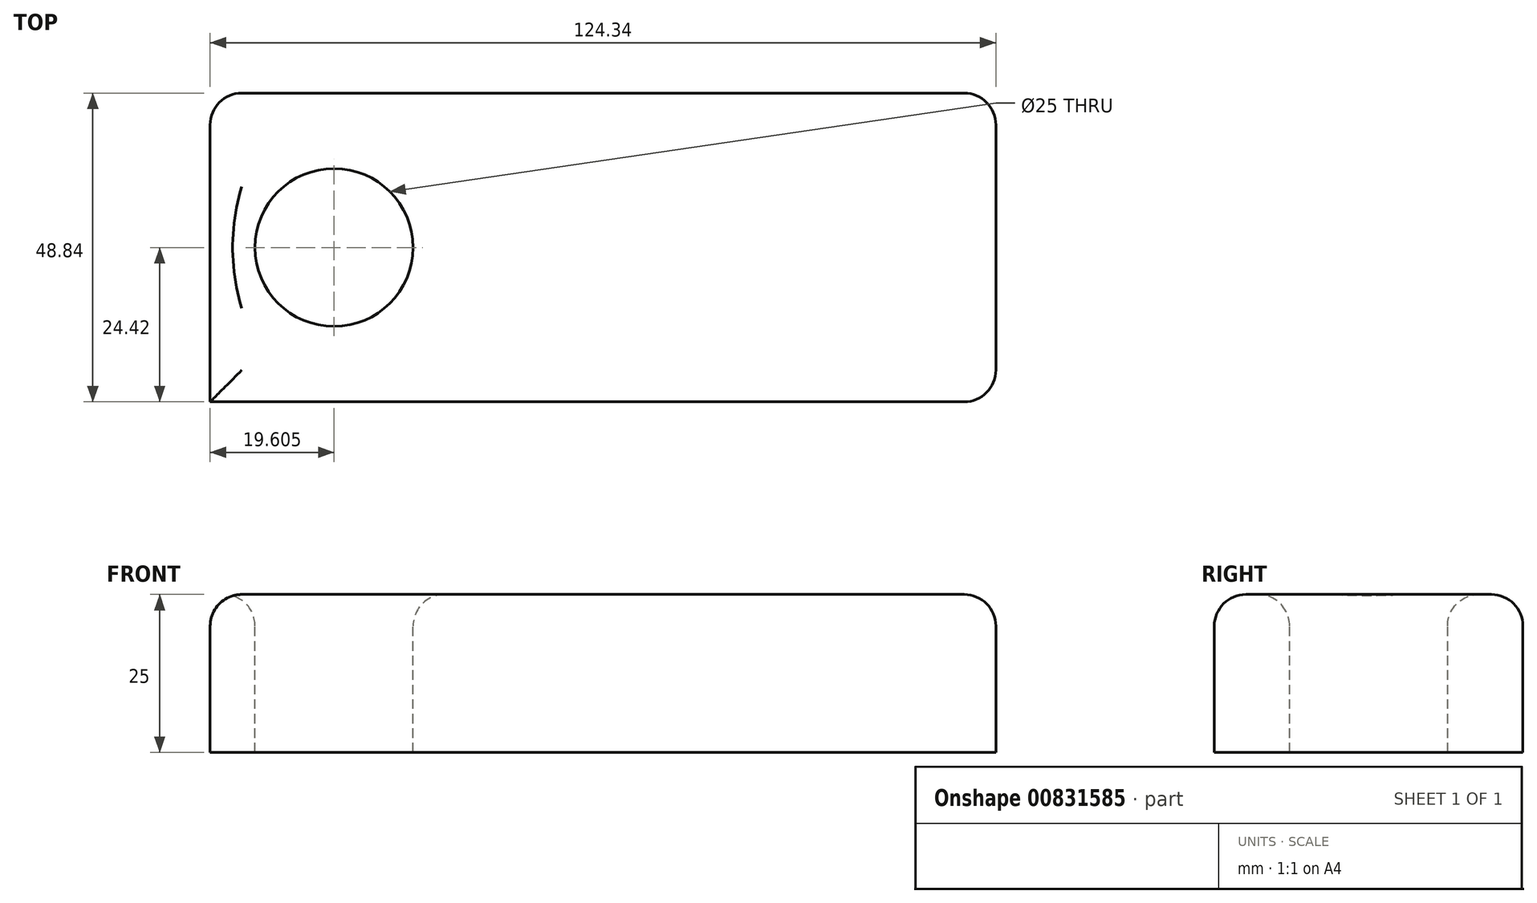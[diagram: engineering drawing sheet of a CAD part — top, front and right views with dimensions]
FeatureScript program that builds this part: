
annotation { "Feature Type Name" : "Feature", "Feature Type Description" : "" }
export const myFeature = defineFeature(function(context is Context, id is Id, definition is map)
    precondition{}
    {
        {
            var Q0;
            Q0=qCreatedBy(makeId("Top.planeOp"),FACE);
            var sketch = newSketch(context, id + "F0", { "sketchPlane" : qUnion([Q0])});
            skLineSegment(sketch, "E0.bottom", {"start": v(-88, 24.42) * mm, "end": v(36.34, 24.42) * mm});
            skLineSegment(sketch, "E0.top", {"start": v(-88, -24.42) * mm, "end": v(36.34, -24.42) * mm});
            skLineSegment(sketch, "E0.left", {"start": v(-88, 24.42) * mm, "end": v(-88, -24.42) * mm});
            skLineSegment(sketch, "E0.right", {"start": v(36.34, 24.42) * mm, "end": v(36.34, -24.42) * mm});
            skSolve(sketch);
        }
        {
            var Q0;
            Q0=makeQuery(id+"F0.imprint","IMPRINT",FACE,{"disambiguationData":[TD([[makeQuery(id+"F0.imprint","IMPRINT",EDGE,{"derivedFrom":sQuery(id+"F0.wireOp",EDGE,"E0.bottom")}),-1.0]])]});
            extrude(context, id + "F1", {"entities" : qUnion([Q0]), "depth" : 25 * mm, "offsetDistance" : 25 * mm});
        }
        {
            var Q0;
            Q0=makeQuery(id+"F1.opExtrude","CAP_FACE",FACE,{"disambiguationData":[OSD([sQuery(id+"F0.wireOp",EDGE,"E0.bottom"),sQuery(id+"F0.wireOp",EDGE,"E0.top"),sQuery(id+"F0.wireOp",EDGE,"E0.left"),sQuery(id+"F0.wireOp",EDGE,"E0.right")])],"isStart":false});
            var sketch = newSketch(context, id + "F2", { "sketchPlane" : qUnion([Q0])});
            skCircle(sketch, "E1", {"center": v(-68.4, 0) * mm, "radius": 13.3 * mm});
            skSolve(sketch);
        }
        {
            var Q0;
            Q0=sQuery(id+"F2.wireOp",VERTEX,"E1.center");
            var Q1;
            Q1=makeQuery(id+"F1.opExtrude","SWEPT_BODY",BODY,{"disambiguationData":[OSD([sQuery(id+"F0.wireOp",EDGE,"E0.bottom"),sQuery(id+"F0.wireOp",EDGE,"E0.top"),sQuery(id+"F0.wireOp",EDGE,"E0.left"),sQuery(id+"F0.wireOp",EDGE,"E0.right")])]});
            hole(context, id + "F3", {"style" : HoleStyle.SIMPLE, "endStyle" : HoleEndStyle.THROUGH, "holeDiameter" : 25 * mm, "majorDiameter" : 5 * mm, "isTappedThrough" : true, "tappedDepth" : 12 * mm, "tapClearance" : 3, "locations" : qUnion([Q0]), "scope" : qUnion([Q1])});
        }
        {
            var Q0;
            Q0=makeQuery(id+"F1.opExtrude","CAP_FACE",FACE,{"disambiguationData":[OSD([sQuery(id+"F0.wireOp",EDGE,"E0.bottom"),sQuery(id+"F0.wireOp",EDGE,"E0.top"),sQuery(id+"F0.wireOp",EDGE,"E0.left"),sQuery(id+"F0.wireOp",EDGE,"E0.right")])],"isStart":false});
            var Q1;
            Q1=makeQuery(id+"F1.opExtrude","CAP_EDGE",EDGE,{"disambiguationData":[OSD([sQuery(id+"F0.wireOp",EDGE,"E0.left")])],"isStart":false});
            var Q2;
            Q2=makeQuery(id+"F1.opExtrude","CAP_EDGE",EDGE,{"disambiguationData":[OSD([sQuery(id+"F0.wireOp",EDGE,"E0.bottom")])],"isStart":false});
            fillet(context, id + "F4", {"entities" : qUnion([Q0, Q1, Q2]), "radius" : 5 * mm, "tangentPropagation" : true, "allowEdgeOverflow" : false});
        }
        {
            var Q0;
            Q0=makeQuery(id+"F1.opExtrude","SWEPT_EDGE",EDGE,{"disambiguationData":[OSD([sQuery(id+"F0.wireOp",EDGE,"E0.top"),sQuery(id+"F0.wireOp",EDGE,"E0.right")])]});
            fillet(context, id + "F5", {"entities" : qUnion([Q0]), "radius" : 5 * mm, "tangentPropagation" : true, "allowEdgeOverflow" : false});
        }
        {
            var Q0;
            Q0=makeQuery(id+"F1.opExtrude","SWEPT_EDGE",EDGE,{"disambiguationData":[OSD([sQuery(id+"F0.wireOp",EDGE,"E0.bottom"),sQuery(id+"F0.wireOp",EDGE,"E0.left")])]});
            var Q1;
            Q1=makeQuery(id+"F1.opExtrude","SWEPT_EDGE",EDGE,{"disambiguationData":[OSD([sQuery(id+"F0.wireOp",EDGE,"E0.bottom"),sQuery(id+"F0.wireOp",EDGE,"E0.right")])]});
            fillet(context, id + "F6", {"entities" : qUnion([Q0, Q1]), "radius" : 5 * mm, "tangentPropagation" : true, "allowEdgeOverflow" : false});
        }
    });
